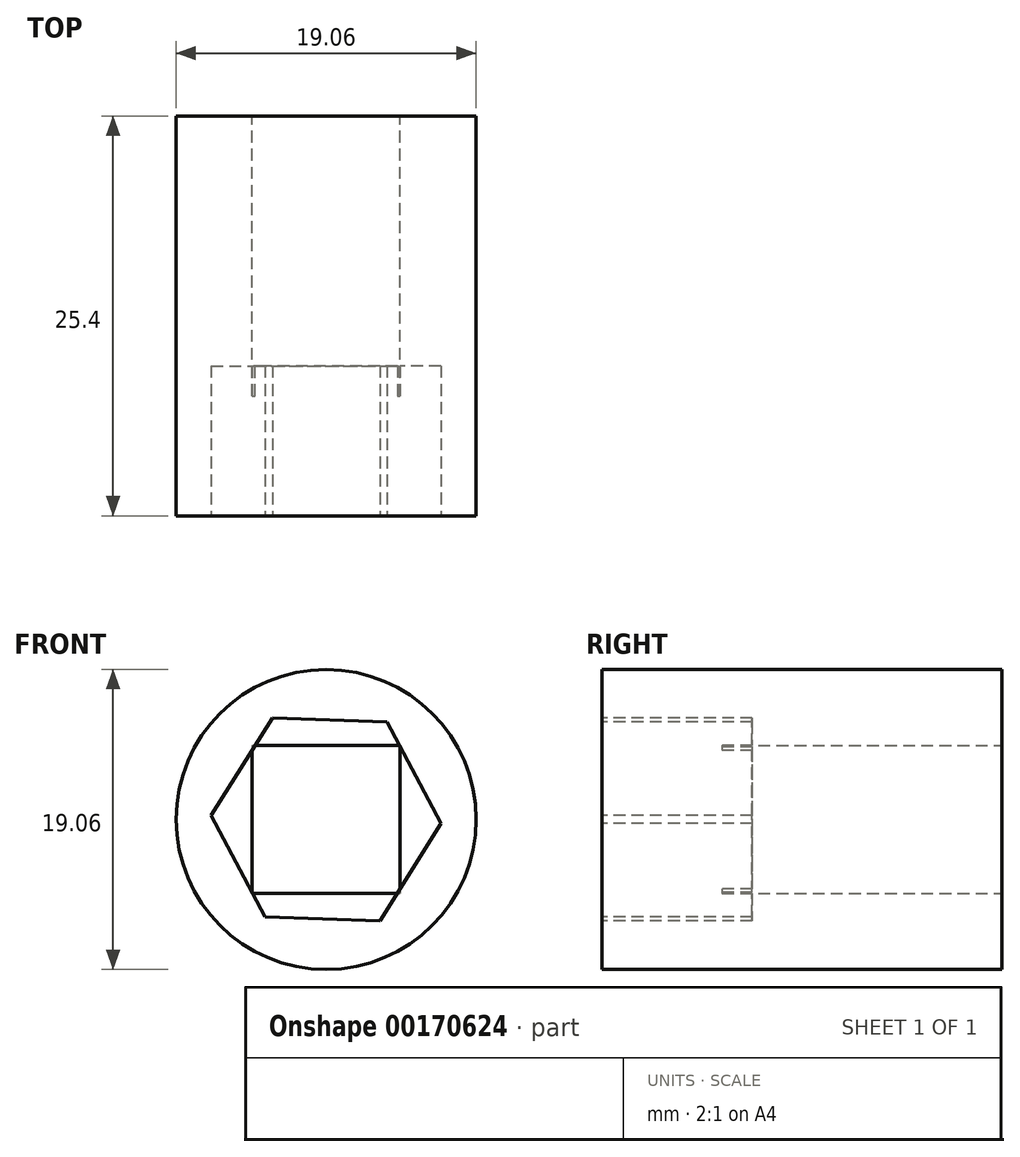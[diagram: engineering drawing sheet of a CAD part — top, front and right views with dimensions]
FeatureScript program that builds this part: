
annotation { "Feature Type Name" : "Feature", "Feature Type Description" : "" }
export const myFeature = defineFeature(function(context is Context, id is Id, definition is map)
    precondition{}
    {
        {
            var Q0;
            Q0=qCreatedBy(makeId("Front.planeOp"),FACE);
            var sketch = newSketch(context, id + "F0", { "sketchPlane" : qUnion([Q0])});
            skCircle(sketch, "E0", {"center": v(0, 0) * mm, "radius": 9.53 * mm});
            skSolve(sketch);
        }
        {
            var Q0;
            Q0=qCreatedBy(makeId("Front.planeOp"),FACE);
            var sketch = newSketch(context, id + "F1", { "sketchPlane" : qUnion([Q0])});
            skLineSegment(sketch, "E1.bottom", {"start": v(-4.7, 4.7) * mm, "end": v(4.7, 4.7) * mm});
            skLineSegment(sketch, "E1.top", {"start": v(-4.7, -4.7) * mm, "end": v(4.7, -4.7) * mm});
            skLineSegment(sketch, "E1.left", {"start": v(-4.7, 4.7) * mm, "end": v(-4.7, -4.7) * mm});
            skLineSegment(sketch, "E1.right", {"start": v(4.7, 4.7) * mm, "end": v(4.7, -4.7) * mm});
            skPoint(sketch, "E1.middle", {"position": v(0, 0) * mm});
            skCircle(sketch, "E2", {"center": v(0, 0) * mm, "radius": 4.7 * mm});
            skSolve(sketch);
        }
        {
            var Q0;
            Q0=makeQuery(id+"F0.imprint","IMPRINT",FACE,{"disambiguationData":[TD([[makeQuery(id+"F0.imprint","IMPRINT",EDGE,{"derivedFrom":sQuery(id+"F0.wireOp",EDGE,"E0")}),1.0]])]});
            var Q1;
            Q1=sQuery(id+"F0.wireOp",EDGE,"E0");
            extrude(context, id + "F2", {"entities" : qUnion([Q0]), "surfaceEntities" : qUnion([Q1]), "depth" : 25.4 * mm});
        }
        {
            var Q0;
            {var subQ0=sQuery(id+"F1.wireOp",EDGE,"E2");var subQ1=makeQuery(id+"F1.imprint","INTERSECT",VERTEX,{"derivedFrom":[sQuery(id+"F1.wireOp",EDGE,"E1.bottom"),subQ0]});Q0=makeQuery(id+"F1.imprint","IMPRINT",FACE,{"disambiguationData":[TD([[makeQuery(id+"F1.imprint","IMPRINT",EDGE,{"disambiguationData":[TD([[subQ1,1.0]])],"derivedFrom":subQ0}),1.0]])]});}
            var Q1;
            Q1=sQuery(id+"F1.wireOp",EDGE,"E2");
            var Q2;
            Q2=qCreatedBy(makeId("Front.planeOp"),FACE);
            extrude(context, id + "F3", {"entities" : qUnion([Q0]), "operationType" : NewBodyOperationType.REMOVE, "surfaceEntities" : qUnion([Q1]), "endBound" : BoundingType.THROUGH_ALL, "endBoundEntityFace" : qUnion([Q2]), "depth" : 25.4 * mm});
        }
        {
            var Q0;
            Q0 = qSketchRegion(id + "F1", true);
            extrude(context, id + "F4", {"entities" : qUnion([Q0]), "operationType" : NewBodyOperationType.REMOVE, "depth" : 17.78 * mm});
        }
        {
            var Q0;
            Q0=makeQuery(id+"F2.opExtrude","CAP_FACE",FACE,{"disambiguationData":[OSD([sQuery(id+"F0.wireOp",EDGE,"E0")])],"isStart":false});
            var sketch = newSketch(context, id + "F5", { "sketchPlane" : qUnion([Q0])});
            skCircle(sketch, "E3.cCircle", {"center": v(0, 0) * mm, "radius": 6.32 * mm, "construction": true});
            skLineSegment(sketch, "E3.0", {"start": v(7.3, -0.26) * mm, "end": v(3.42, -6.45) * mm});
            skLineSegment(sketch, "E3.1", {"start": v(3.42, -6.45) * mm, "end": v(-3.88, -6.19) * mm});
            skLineSegment(sketch, "E3.2", {"start": v(-3.88, -6.19) * mm, "end": v(-7.3, 0.26) * mm});
            skLineSegment(sketch, "E3.3", {"start": v(-7.3, 0.26) * mm, "end": v(-3.42, 6.45) * mm});
            skLineSegment(sketch, "E3.4", {"start": v(-3.42, 6.45) * mm, "end": v(3.88, 6.19) * mm});
            skLineSegment(sketch, "E3.5", {"start": v(3.88, 6.19) * mm, "end": v(7.3, -0.26) * mm});
            skPoint(sketch, "E3.0.midPoint", {"position": v(5.36, -3.36) * mm});
            skSolve(sketch);
        }
        {
            var Q0;
            Q0 = qSketchRegion(id + "F5", true);
            extrude(context, id + "F6", {"entities" : qUnion([Q0]), "operationType" : NewBodyOperationType.REMOVE, "oppositeDirection" : true, "depth" : 9.52 * mm});
        }
    });
